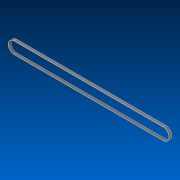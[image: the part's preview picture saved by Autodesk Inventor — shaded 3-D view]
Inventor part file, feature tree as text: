
AUTODESK INVENTOR PART (.ipt)
format: ipt  version: 2022.2 (Build 262287000, 287)  size: 91,136 bytes
history: native  units: in
note: dims shown in document units (in); Inventor stores cm internally (conversion verified against a paired STEP export)
features: extrude x1, sketch x1
ambient origin geometry x8: Origin, YZ Plane, XZ Plane, XY Plane, X Axis, Y Axis, Z Axis, Center Point
bodies: Solid1 (feature_tree)
feature tree (2):
  extrude  "Extrusion1"  Depth=1.504in
  sketch  "Sketch1"  dims[d0=19.5in d1=1.504in d2=0.0394in d3=0.3543in d4=0.0in]
